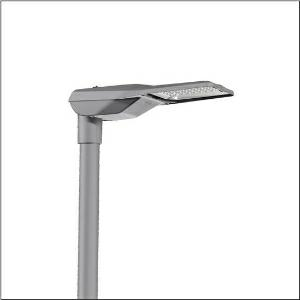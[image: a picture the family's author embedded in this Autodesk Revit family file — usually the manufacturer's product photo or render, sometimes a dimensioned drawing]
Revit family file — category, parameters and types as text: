
# Revit family: streetlight_sl_21_mini___st1_5a_5xe2p43s08gb_b57c
name_source: partatom
category: Lighting Fixtures
units: mm (PartAtom-declared; Revit-internal decimal feet)

## family parameters
Cut with Voids When Loaded = No
Host = Face
Light Source = No
Part Type = Normal
Room Calculation Point = No
Round Connector Dimension = Use Diameter
Shared = No

## types (1)
- --- (1 x LED, 6080 lm, 40.4 W, 4000K)
    Apparent Load = 40 VA
    CIE Flux Codes = 22 53 95 100 100
    Color Rendering = 70
    Color Temperature = 4000K
    Default Elevation = 1800 mm
    Description = Streetlight SL 21 mini, mast luminaire, primary light control with lens, of PMMA, primary optical cover: cover, of toughened safety glass, transparent, light distribution: ST1.5a, light emission: direct distribution, primary light characteristic: asymmetric, installation type: side-entry, post-top, LED, High Power LED, rated luminous flux: 6.080lm, luminous efficacy: 151lm/W, light colour: 740, colour temperature: 4000K, control gear: D4i, control: overheat protection, constant luminous flux control, time-dependent luminous flux control, flexible luminous flux parameterisation, pre-setting: logarithmic dimming characteristic, mains connection: 220..240V, AC, 50/60Hz, start of lifetime: 40W, end of service life: 41W, reduction: 19W, luminaire housing, of diecast aluminium, powder-coated, SITECO metallic grey (DB 702S), corrosivity category C5 high according to DIN EN ISO 12944, please order mast flange separately, inclination adjustable: 0°, 5°, 10°, 15°, sealing non-destructively replaceable, multi-level sealing system, length: 628mm, width: 235mm, height: 110mm, mast flange for spigot size: 42mm (side-entry): 5XC10008XM4, 60/48mm (side-entry/post-top): 5XC10108XM2, 76/60mm (side-entry/post-top): 5XC10108XM1, mounting height: 4..8m, Smart Interface above, protection rating (complete): IP66, insulation class (complete): insulation class II (safety insulation), certification: CE, ENEC, ENEC+, VDE, impact resistance: IK10, permissible operating ambient temperature for outdoor applications: -40..+50°C, standard-compliant lighting for roads and squares, packaging unit: 1 piece

Light Distribution: ST1.5a
    Height = 110 mm
    Lamp = 1 x LED
    Lamp Light Flux = 6080 lm
    Lamp Power = 40.4 W
    Lamp count = 1
    Length = 625 mm
    Luminous efficacy = 151 lm/W
    Manufacturer = Siteco
    ModVariant = No
    Model = 5XE2P43S08GB
    Number of Poles = 1
    OnlyDefault = Yes
    Power Factor = 1
    Product Name = Streetlight SL 21 mini | ST1.5a
    Product group = mast luminaire | pylon top
    ProductGroupID = 6100
    Protection Class = Protection class II
    Protection Degree = IP 66
    RLX_Detail_Level = 1
    RLX_Emergency_Light_Flux = 0 lm
    RLX_Emergency_Type = 0
    RLX_Emergency_Type_DB = No
    RlxData = <blob elided: 29705 chars, md5=9dbf99b9>
    Socket = socket
    Standby Power = 0 W
    System Light Flux = 6080 lm
    System Power = 40 W
    Type Comments = factory setting: luminous flux: 100 % | dim-lin: 254 | 812 mA
    Type Image = l_1003515.jpg
    URL = http://relux.com
    VarID = @adj_175161
    Voltage = 0 V
    Weight = 0.00 kg
    Width = 234 mm

## geometry (parser evidence)
native form markers: Blend x4, Sweep x9
no freeform markers — native parametric forms only
